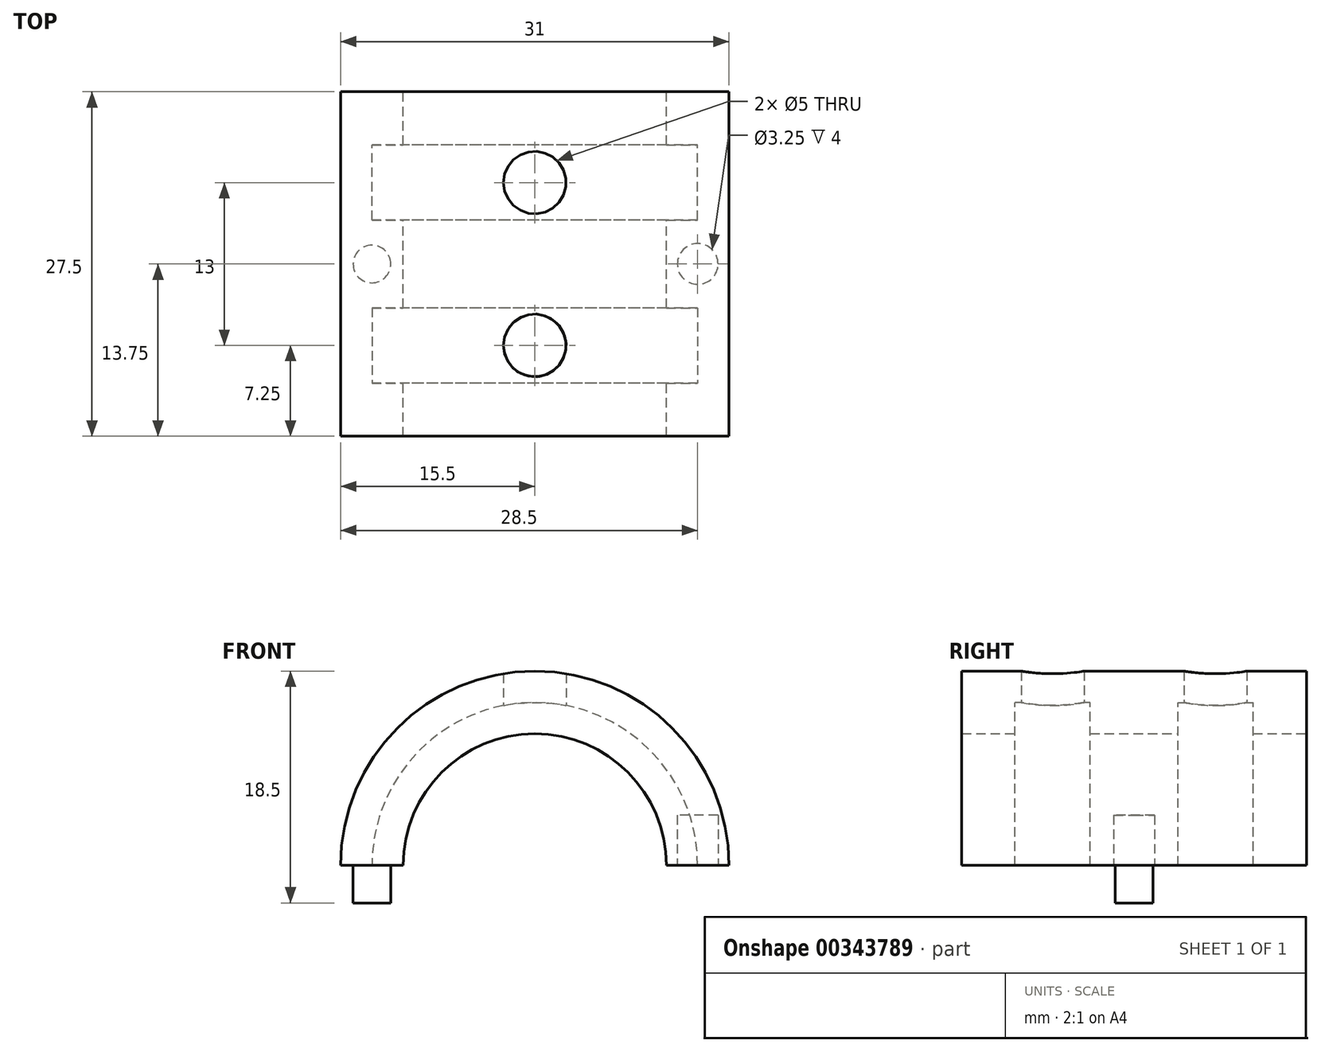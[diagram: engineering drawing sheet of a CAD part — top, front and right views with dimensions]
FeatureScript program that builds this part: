
annotation { "Feature Type Name" : "Feature", "Feature Type Description" : "" }
export const myFeature = defineFeature(function(context is Context, id is Id, definition is map)
    precondition{}
    {
        {
            var Q0;
            Q0=qCreatedBy(makeId("Front.planeOp"),FACE);
            var sketch = newSketch(context, id + "F0", { "sketchPlane" : qUnion([Q0])});
            skArc(sketch, "E0", {"start": v(10.5, 0) * mm, "mid": v(0, 10.5) * mm, "end": v(-10.5, 0) * mm});
            skArc(sketch, "E1", {"start": v(15.5, 0) * mm, "mid": v(0, 15.5) * mm, "end": v(-15.5, 0) * mm});
            skLineSegment(sketch, "E2", {"start": v(-15.5, 0) * mm, "end": v(-10.5, 0) * mm});
            skLineSegment(sketch, "E3", {"start": v(10.5, 0) * mm, "end": v(15.5, 0) * mm});
            skSolve(sketch);
        }
        {
            var Q0;
            {var subQ0=sQuery(id+"F0.wireOp",EDGE,"E1");Q0=makeQuery(id+"F0.imprint","IMPRINT",FACE,{"disambiguationData":[TD([[makeQuery(id+"F0.imprint","IMPRINT",EDGE,{"derivedFrom":subQ0}),1.0]])]});}
            var Q1;
            {var subQ0=sQuery(id+"F0.wireOp",EDGE,"E0");Q1=makeQuery(id+"F0.imprint","IMPRINT",FACE,{"disambiguationData":[TD([[makeQuery(id+"F0.imprint","IMPRINT",EDGE,{"derivedFrom":subQ0}),-1.0]])]});}
            extrude(context, id + "F1", {"entities" : qUnion([Q0, Q1]), "depth" : 27.5 * mm, "offsetDistance" : 25 * mm, "symmetric" : true});
        }
        {
            var Q0;
            Q0=qCreatedBy(makeId("Top.planeOp"),FACE);
            var sketch = newSketch(context, id + "F2", { "sketchPlane" : qUnion([Q0])});
            skCircle(sketch, "E4", {"center": v(0, 6.5) * mm, "radius": 2.5 * mm});
            skCircle(sketch, "E5", {"center": v(0, -6.5) * mm, "radius": 2.5 * mm});
            skSolve(sketch);
        }
        {
            var Q0;
            Q0 = qSketchRegion(id + "F2", true);
            extrude(context, id + "F3", {"entities" : qUnion([Q0]), "operationType" : NewBodyOperationType.REMOVE, "depth" : 30.7 * mm, "offsetDistance" : 25 * mm});
        }
        {
            var Q0;
            Q0=qCreatedBy(makeId("Front.planeOp"),FACE);
            var sketch = newSketch(context, id + "F4", { "sketchPlane" : qUnion([Q0])});
            skSolve(sketch);
        }
        {
            var Q0;
            Q0=qCreatedBy(makeId("Top.planeOp"),FACE);
            var sketch = newSketch(context, id + "F5", { "sketchPlane" : qUnion([Q0])});
            skCircle(sketch, "E6", {"center": v(-13, 0) * mm, "radius": 1.5 * mm});
            skCircle(sketch, "E7", {"center": v(13, 0) * mm, "radius": 1.63 * mm});
            skSolve(sketch);
        }
        {
            var Q0;
            Q0=makeQuery(id+"F5.imprint","IMPRINT",FACE,{"disambiguationData":[TD([[makeQuery(id+"F5.imprint","IMPRINT",EDGE,{"derivedFrom":sQuery(id+"F5.wireOp",EDGE,"E6")}),1.0]])]});
            extrude(context, id + "F6", {"entities" : qUnion([Q0]), "operationType" : NewBodyOperationType.ADD, "oppositeDirection" : true, "depth" : 3 * mm, "offsetDistance" : 25 * mm});
        }
        {
            var Q0;
            Q0=makeQuery(id+"F5.imprint","IMPRINT",FACE,{"disambiguationData":[TD([[makeQuery(id+"F5.imprint","IMPRINT",EDGE,{"derivedFrom":sQuery(id+"F5.wireOp",EDGE,"E7")}),1.0]])]});
            extrude(context, id + "F7", {"entities" : qUnion([Q0]), "operationType" : NewBodyOperationType.REMOVE, "depth" : 4 * mm, "offsetDistance" : 25 * mm});
        }
        {
            var Q0;
            Q0 = qBodyType(qCreatedBy(id + "F4" ,EDGE), BodyType.WIRE);
            var Q1;
            Q1=qCreatedBy(makeId("Front.planeOp"),FACE);
            cPlane(context, id + "F8", {"entities" : qUnion([Q0, Q1]), "cplaneType" : CPlaneType.OFFSET, "offset" : 6.5 * mm, "width" : 150 * mm, "height" : 150 * mm});
        }
        {
            var Q0;
            Q0=qCreatedBy(id+"F8.planeOp",FACE);
            var sketch = newSketch(context, id + "F9", { "sketchPlane" : qUnion([Q0])});
            skCircle(sketch, "E8", {"center": v(0, 0) * mm, "radius": 13 * mm});
            skCircle(sketch, "E9", {"center": v(0, 0) * mm, "radius": 10.5 * mm});
            skSolve(sketch);
        }
        {
            var Q0;
            Q0 = qSketchRegion(id + "F9", true);
            extrude(context, id + "F10", {"entities" : qUnion([Q0]), "operationType" : NewBodyOperationType.REMOVE, "oppositeDirection" : true, "depth" : 6 * mm, "offsetDistance" : 25 * mm, "symmetric" : true});
        }
        {
            var Q0;
            Q0=qCreatedBy(makeId("Front.planeOp"),FACE);
            cPlane(context, id + "F11", {"entities" : qUnion([Q0]), "cplaneType" : CPlaneType.OFFSET, "offset" : 6.5 * mm, "oppositeDirection" : true, "width" : 150 * mm, "height" : 150 * mm});
        }
        {
            var Q0;
            Q0=qCreatedBy(id+"F11.planeOp",FACE);
            var sketch = newSketch(context, id + "F12", { "sketchPlane" : qUnion([Q0])});
            skCircle(sketch, "E10", {"center": v(0, 0) * mm, "radius": 13 * mm});
            skCircle(sketch, "E11", {"center": v(0, 0) * mm, "radius": 10.5 * mm});
            skSolve(sketch);
        }
        {
            var Q0;
            Q0 = qSketchRegion(id + "F12", true);
            extrude(context, id + "F13", {"entities" : qUnion([Q0]), "operationType" : NewBodyOperationType.REMOVE, "depth" : 6 * mm, "offsetDistance" : 25 * mm, "symmetric" : true});
        }
    });
